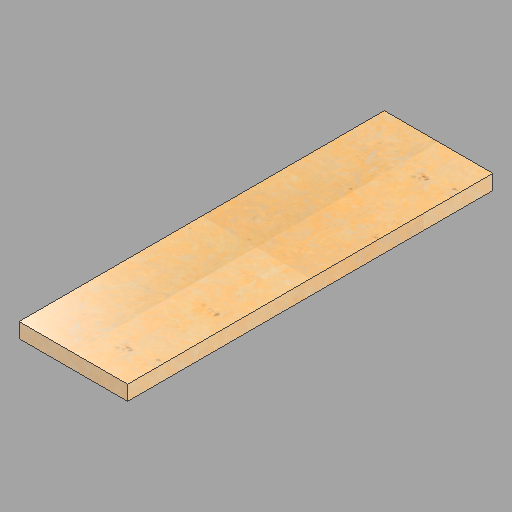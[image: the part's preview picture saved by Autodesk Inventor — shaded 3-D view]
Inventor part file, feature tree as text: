
AUTODESK INVENTOR PART (.ipt)
format: ipt  version: 2022.2 (Build 262287010, 287A)  size: 223,744 bytes
history: native  units: in
note: dims shown in document units (in); Inventor stores cm internally (conversion verified against a paired STEP export)
features: extrude x2, sketch x1
ambient origin geometry x8: Origin, YZ Plane, XZ Plane, XY Plane, X Axis, Y Axis, Z Axis, Center Point
bodies: Solid1 (feature_tree)
feature tree (3):
  sketch  "Sketch1"  dims[d2=22.0in d3=74.0in d4=0.375in d5=0.25in d6=3.0in d7=0.0in d11=0.25in d12=0.0in]
  extrude  "Extrusion1"  Depth=74.0in
  extrude  "Extrusion3"  Depth=0.375in
